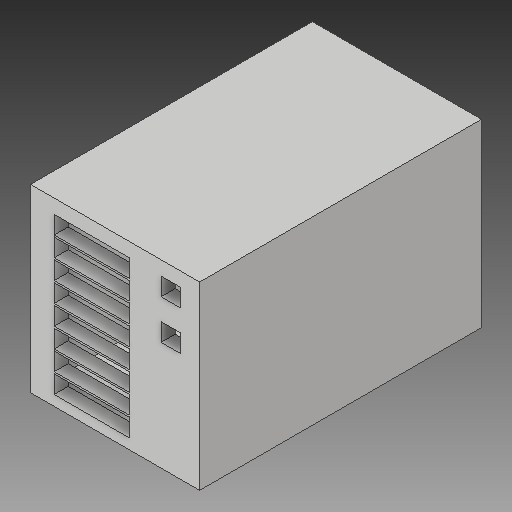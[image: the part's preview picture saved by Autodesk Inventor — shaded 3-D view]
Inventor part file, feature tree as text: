
AUTODESK INVENTOR PART (.ipt)
format: ipt  version: 2017 (Build 210142000, 142)  size: 180,736 bytes
history: native  units: in
note: dims shown in document units (in); Inventor stores cm internally (conversion verified against a paired STEP export)
features: extrude x2, sketch x2, shell x1
ambient origin geometry x8: Origin, YZ Plane, XZ Plane, XY Plane, X Axis, Y Axis, Z Axis, Center Point
bodies: Solid1 (feature_tree)
feature tree (5):
  extrude  "Extrusion1"  Depth=5.0394in
  extrude  "Extrusion2"  Depth=0.5in
  shell  "Shell1"  Thickness=0.3937in
  sketch  "Sketch1"  dims[d0=4.7244in d1=5.0394in]
  sketch  "Sketch2"  dims[d2=7.874in d3=0.0in d4=0.5in d5=0.3937in d6=2.0945in d8=1.9685in d9=3.1496in d11=0.5512in d12=0.3937in d14=0.3937in d16=0.3937in d17=0.0in d18=0.0787in]
